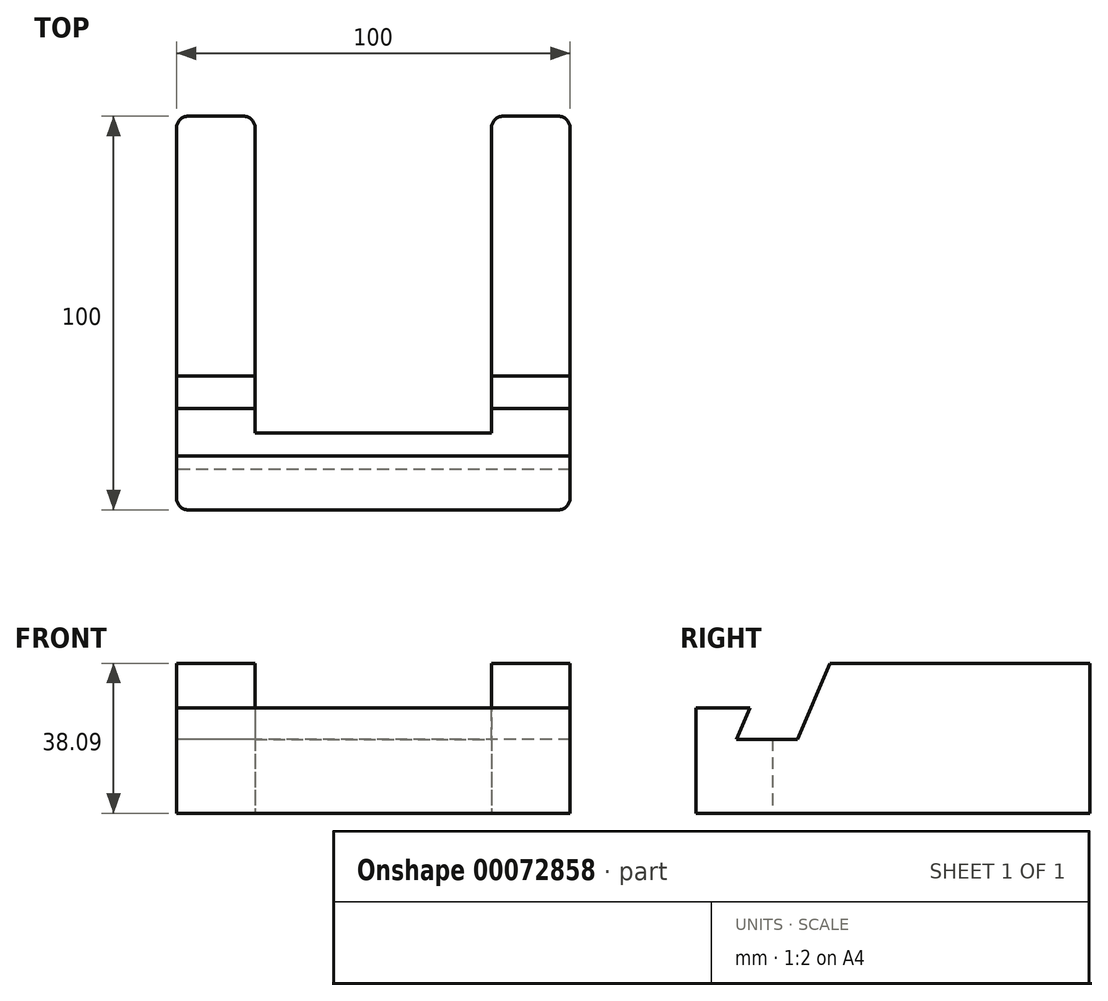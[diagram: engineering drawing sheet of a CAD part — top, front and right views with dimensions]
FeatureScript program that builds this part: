
annotation { "Feature Type Name" : "Feature", "Feature Type Description" : "" }
export const myFeature = defineFeature(function(context is Context, id is Id, definition is map)
    precondition{}
    {
        {
            var Q0;
            Q0=qCreatedBy(makeId("Top.planeOp"),FACE);
            var sketch = newSketch(context, id + "F0", { "sketchPlane" : qUnion([Q0])});
            skLineSegment(sketch, "E0.bottom", {"start": v(-61.88, 57.97) * mm, "end": v(-47.88, 57.97) * mm});
            skLineSegment(sketch, "E0.top", {"start": v(-61.88, -42.03) * mm, "end": v(32.12, -42.03) * mm});
            skLineSegment(sketch, "E0.left", {"start": v(-64.88, 54.97) * mm, "end": v(-64.88, -39.03) * mm});
            skLineSegment(sketch, "E0.right", {"start": v(35.12, 54.97) * mm, "end": v(35.12, -39.03) * mm});
            skLineSegment(sketch, "E1", {"start": v(-44.88, 54.97) * mm, "end": v(-44.88, -22.57) * mm});
            skLineSegment(sketch, "E2", {"start": v(-44.88, -22.57) * mm, "end": v(15.12, -22.57) * mm});
            skLineSegment(sketch, "E3", {"start": v(15.12, -22.57) * mm, "end": v(15.12, 54.97) * mm});
            skLineSegment(sketch, "E4.trimOffspring", {"start": v(18.12, 57.97) * mm, "end": v(32.12, 57.97) * mm});
            skPoint(sketch, "E5.visualSharp", {"position": v(-64.88, 57.97) * mm});
            skArc(sketch, "E5.filletArc", {"start": v(-61.88, 57.97) * mm, "mid": v(-64, 57.09) * mm, "end": v(-64.88, 54.97) * mm});
            skPoint(sketch, "E6.visualSharp", {"position": v(15.12, 57.97) * mm});
            skArc(sketch, "E6.filletArc", {"start": v(18.12, 57.97) * mm, "mid": v(16, 57.09) * mm, "end": v(15.12, 54.97) * mm});
            skPoint(sketch, "E7.visualSharp", {"position": v(35.12, 57.97) * mm});
            skArc(sketch, "E7.filletArc", {"start": v(35.12, 54.97) * mm, "mid": v(34.24, 57.09) * mm, "end": v(32.12, 57.97) * mm});
            skPoint(sketch, "E8.visualSharp", {"position": v(35.12, -42.03) * mm});
            skArc(sketch, "E8.filletArc", {"start": v(32.12, -42.03) * mm, "mid": v(34.24, -41.15) * mm, "end": v(35.12, -39.03) * mm});
            skPoint(sketch, "E9.visualSharp", {"position": v(-64.88, -42.03) * mm});
            skArc(sketch, "E9.filletArc", {"start": v(-64.88, -39.03) * mm, "mid": v(-64, -41.15) * mm, "end": v(-61.88, -42.03) * mm});
            skPoint(sketch, "E10.visualSharp", {"position": v(-44.88, 57.97) * mm});
            skArc(sketch, "E10.filletArc", {"start": v(-44.88, 54.97) * mm, "mid": v(-45.76, 57.09) * mm, "end": v(-47.88, 57.97) * mm});
            skSolve(sketch);
        }
        {
            var Q0;
            Q0=makeQuery(id+"F0.imprint","IMPRINT",FACE,{"disambiguationData":[TD([[makeQuery(id+"F0.imprint","IMPRINT",EDGE,{"derivedFrom":sQuery(id+"F0.wireOp",EDGE,"E0.bottom")}),-1.0]])]});
            extrude(context, id + "F1", {"entities" : qUnion([Q0]), "depth" : 38.1 * mm});
        }
        {
            var Q0;
            Q0=qCreatedBy(makeId("Right.planeOp"),FACE);
            var sketch = newSketch(context, id + "F2", { "sketchPlane" : qUnion([Q0])});
            skLineSegment(sketch, "E11", {"start": v(-86.84, 51.99) * mm, "end": v(-102.24, 16.37) * mm});
            skLineSegment(sketch, "E12", {"start": v(-102.24, 16.37) * mm, "end": v(-86.81, 16.37) * mm});
            skLineSegment(sketch, "E13", {"start": v(-86.81, 16.37) * mm, "end": v(-71.41, 51.99) * mm});
            skLineSegment(sketch, "E14", {"start": v(-71.41, 51.99) * mm, "end": v(-86.84, 51.99) * mm});
            skSolve(sketch);
        }
        {
            var Q0;
            Q0 = qSketchRegion(id + "F2", true);
            extrude(context, id + "F3", {"entities" : qUnion([Q0]), "depth" : 122.49 * mm});
        }
        {
            var Q0;
            Q0=makeQuery(id+"F3.opExtrude","SWEPT_BODY",BODY,{"disambiguationData":[OSD([sQuery(id+"F2.wireOp",EDGE,"E11"),sQuery(id+"F2.wireOp",EDGE,"E12"),sQuery(id+"F2.wireOp",EDGE,"E13"),sQuery(id+"F2.wireOp",EDGE,"E14")])]});
            transform(context, id + "F4", {"entities" : qUnion([Q0]), "transformType" : TransformType.TRANSLATION_3D, "dx" : -76.72 * mm, "dy" : 70.5 * mm, "dz" : 2.45 * mm, "makeCopy" : false});
        }
        {
            var Q0;
            Q0=makeQuery(id+"F3.opExtrude","SWEPT_BODY",BODY,{"disambiguationData":[OSD([sQuery(id+"F2.wireOp",EDGE,"E11"),sQuery(id+"F2.wireOp",EDGE,"E12"),sQuery(id+"F2.wireOp",EDGE,"E13"),sQuery(id+"F2.wireOp",EDGE,"E14")])]});
            var Q1;
            Q1=makeQuery(id+"F1.opExtrude","SWEPT_BODY",BODY,{"disambiguationData":[OSD([sQuery(id+"F0.wireOp",EDGE,"E0.bottom"),sQuery(id+"F0.wireOp",EDGE,"E0.top"),sQuery(id+"F0.wireOp",EDGE,"E0.left"),sQuery(id+"F0.wireOp",EDGE,"E0.right"),sQuery(id+"F0.wireOp",EDGE,"E1"),sQuery(id+"F0.wireOp",EDGE,"E2"),sQuery(id+"F0.wireOp",EDGE,"E3"),sQuery(id+"F0.wireOp",EDGE,"E4.trimOffspring"),sQuery(id+"F0.wireOp",EDGE,"E5.filletArc"),sQuery(id+"F0.wireOp",EDGE,"E6.filletArc"),sQuery(id+"F0.wireOp",EDGE,"E7.filletArc"),sQuery(id+"F0.wireOp",EDGE,"E8.filletArc"),sQuery(id+"F0.wireOp",EDGE,"E9.filletArc"),sQuery(id+"F0.wireOp",EDGE,"E10.filletArc")])]});
            booleanBodies(context, id + "F5", {"operationType" : BooleanOperationType.SUBTRACTION, "tools" : qUnion([Q0]), "targets" : qUnion([Q1])});
        }
        {
            var Q0;
            Q0=qCreatedBy(makeId("Right.planeOp"),FACE);
            var sketch = newSketch(context, id + "F6", { "sketchPlane" : qUnion([Q0])});
            skLineSegment(sketch, "E15.bottom", {"start": v(-63.35, 42.74) * mm, "end": v(-93.45, 42.74) * mm});
            skLineSegment(sketch, "E15.top", {"start": v(-63.35, 26.76) * mm, "end": v(-93.45, 26.76) * mm});
            skLineSegment(sketch, "E15.left", {"start": v(-63.35, 42.74) * mm, "end": v(-63.35, 26.76) * mm});
            skLineSegment(sketch, "E15.right", {"start": v(-93.45, 42.74) * mm, "end": v(-93.45, 26.76) * mm});
            skSolve(sketch);
        }
        {
            var Q0;
            Q0 = qSketchRegion(id + "F6", true);
            extrude(context, id + "F7", {"entities" : qUnion([Q0]), "operationType" : NewBodyOperationType.ADD, "endBound" : BoundingType.SYMMETRIC, "depth" : 152.18 * mm});
        }
        {
            var Q0;
            Q0=makeQuery(id+"F7.opExtrude","SWEPT_BODY",BODY,{"disambiguationData":[OSD([sQuery(id+"F6.wireOp",EDGE,"E15.bottom"),sQuery(id+"F6.wireOp",EDGE,"E15.top"),sQuery(id+"F6.wireOp",EDGE,"E15.left"),sQuery(id+"F6.wireOp",EDGE,"E15.right")])]});
            transform(context, id + "F8", {"entities" : qUnion([Q0]), "transformType" : TransformType.TRANSLATION_3D, "dx" : 0 * mm, "dy" : 44.65 * mm, "dz" : 0 * mm, "makeCopy" : false});
        }
        {
            var Q0;
            Q0=makeQuery(id+"F7.opExtrude","SWEPT_BODY",BODY,{"disambiguationData":[OSD([sQuery(id+"F6.wireOp",EDGE,"E15.bottom"),sQuery(id+"F6.wireOp",EDGE,"E15.top"),sQuery(id+"F6.wireOp",EDGE,"E15.left"),sQuery(id+"F6.wireOp",EDGE,"E15.right")])]});
            var Q1;
            Q1=makeQuery(id+"F1.opExtrude","SWEPT_BODY",BODY,{"disambiguationData":[OSD([sQuery(id+"F0.wireOp",EDGE,"E0.bottom"),sQuery(id+"F0.wireOp",EDGE,"E0.top"),sQuery(id+"F0.wireOp",EDGE,"E0.left"),sQuery(id+"F0.wireOp",EDGE,"E0.right"),sQuery(id+"F0.wireOp",EDGE,"E1"),sQuery(id+"F0.wireOp",EDGE,"E2"),sQuery(id+"F0.wireOp",EDGE,"E3"),sQuery(id+"F0.wireOp",EDGE,"E4.trimOffspring"),sQuery(id+"F0.wireOp",EDGE,"E5.filletArc"),sQuery(id+"F0.wireOp",EDGE,"E6.filletArc"),sQuery(id+"F0.wireOp",EDGE,"E7.filletArc"),sQuery(id+"F0.wireOp",EDGE,"E8.filletArc"),sQuery(id+"F0.wireOp",EDGE,"E9.filletArc"),sQuery(id+"F0.wireOp",EDGE,"E10.filletArc")])]});
            booleanBodies(context, id + "F9", {"operationType" : BooleanOperationType.SUBTRACTION, "tools" : qUnion([Q0]), "targets" : qUnion([Q1])});
        }
    });
